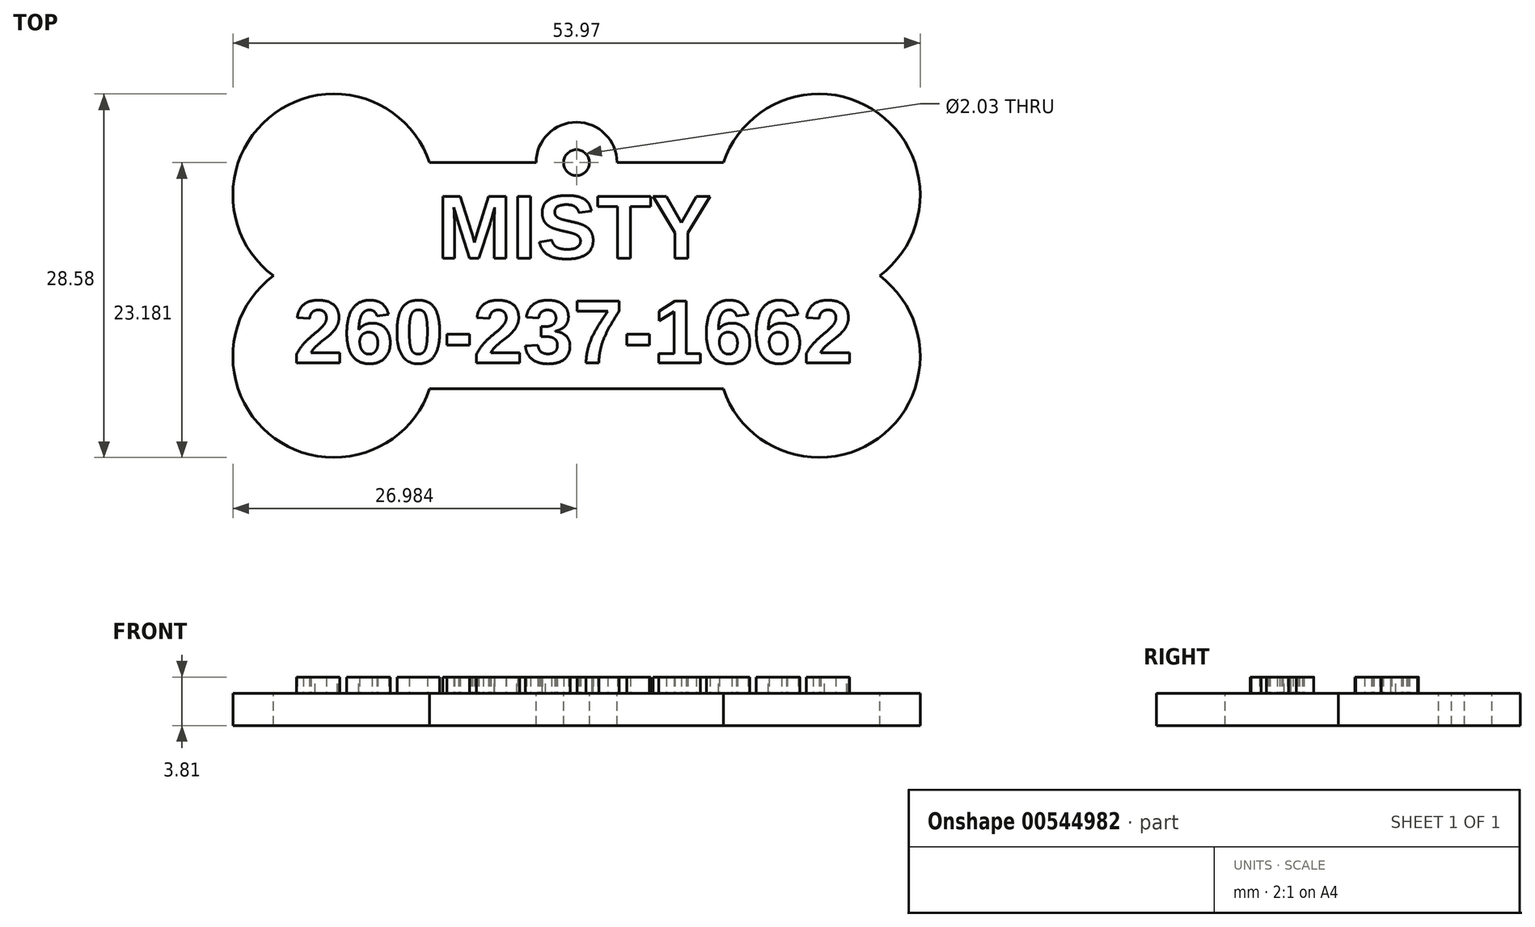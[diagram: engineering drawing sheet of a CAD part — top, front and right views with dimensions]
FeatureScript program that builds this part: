
annotation { "Feature Type Name" : "Feature", "Feature Type Description" : "" }
export const myFeature = defineFeature(function(context is Context, id is Id, definition is map)
    precondition{}
    {
        {
            var Q0;
            Q0=qCreatedBy(makeId("Top.planeOp"),FACE);
            var sketch = newSketch(context, id + "F0", { "sketchPlane" : qUnion([Q0])});
            skArc(sketch, "E0", {"start": v(-23.64, 27.3) * mm, "mid": v(-35.81, 31.18) * mm, "end": v(-35.92, 18.4) * mm});
            skArc(sketch, "E1", {"start": v(11.7, 18.4) * mm, "mid": v(11.6, 31.18) * mm, "end": v(-0.58, 27.3) * mm});
            skArc(sketch, "E2", {"start": v(-35.92, 18.4) * mm, "mid": v(-35.81, 5.62) * mm, "end": v(-23.64, 9.51) * mm});
            skArc(sketch, "E3", {"start": v(-0.58, 9.51) * mm, "mid": v(11.6, 5.62) * mm, "end": v(11.7, 18.4) * mm});
            skArc(sketch, "E4", {"start": v(-8.93, 27.3) * mm, "mid": v(-12.1, 30.47) * mm, "end": v(-15.28, 27.3) * mm});
            skLineSegment(sketch, "E5", {"start": v(-23.64, 27.3) * mm, "end": v(-15.28, 27.3) * mm});
            skLineSegment(sketch, "E6.0", {"start": v(-23.64, 9.51) * mm, "end": v(-0.58, 9.51) * mm});
            skPoint(sketch, "E7.orphan", {"position": v(-31.16, 27.3) * mm});
            skPoint(sketch, "E8.orphan", {"position": v(6.94, 27.3) * mm});
            skLineSegment(sketch, "E9.trimOffspring", {"start": v(-8.93, 27.3) * mm, "end": v(-0.58, 27.3) * mm});
            skCircle(sketch, "E10", {"center": v(-12.1, 27.3) * mm, "radius": 1.02 * mm});
            skSolve(sketch);
        }
        {
            var Q0;
            Q0=qSketchRegion(id+"F0",true);
            extrude(context, id + "F1", {"entities" : qUnion([Q0]), "oppositeDirection" : true, "depth" : 2.54 * mm, "offsetDistance" : 25.4 * mm});
        }
        {
            var Q0;
            Q0=makeQuery(id+"F1.opExtrude","CAP_FACE",FACE,{"disambiguationData":[OSD([sQuery(id+"F0.wireOp",EDGE,"E0"),sQuery(id+"F0.wireOp",EDGE,"E1"),sQuery(id+"F0.wireOp",EDGE,"E2"),sQuery(id+"F0.wireOp",EDGE,"E3"),sQuery(id+"F0.wireOp",EDGE,"E4"),sQuery(id+"F0.wireOp",EDGE,"E5"),sQuery(id+"F0.wireOp",EDGE,"E6.0"),sQuery(id+"F0.wireOp",EDGE,"E9.trimOffspring"),sQuery(id+"F0.wireOp",EDGE,"E10")])],"isStart":true});
            var sketch = newSketch(context, id + "F2", { "sketchPlane" : qUnion([Q0])});
            skText(sketch, "E11", { "text": "MISTY", "fontName": "Arimo-Bold.ttf"});
            const initialGuessF2  = {"E11": [-0.02307, 0.01978, 1, 0, 0.00508]};
            skSetInitialGuess(sketch, initialGuessF2);
            skSolve(sketch);
        }
        {
            var Q0;
            Q0=qSketchRegion(id+"F2",true);
            extrude(context, id + "F3", {"entities" : qUnion([Q0]), "operationType" : NewBodyOperationType.ADD, "depth" : 1.27 * mm, "offsetDistance" : 25.4 * mm});
        }
        {
            var Q0;
            {var subQ0=sQuery(id+"F0.wireOp",EDGE,"E6.0");var subQ1=sQuery(id+"F0.wireOp",EDGE,"E5");var subQ2=sQuery(id+"F0.wireOp",EDGE,"E0");var subQ3=sQuery(id+"F0.wireOp",EDGE,"E4");var subQ4=sQuery(id+"F0.wireOp",EDGE,"E3");var subQ5=sQuery(id+"F0.wireOp",EDGE,"E1");var subQ6=sQuery(id+"F0.wireOp",EDGE,"E2");var subQ7=sQuery(id+"F0.wireOp",EDGE,"E9.trimOffspring");var subQ8=sQuery(id+"F0.wireOp",EDGE,"E10");Q0=makeQuery(id+"F3.boolean.opBoolean","SPLIT",FACE,{"disambiguationData":[TD([makeQuery(id+"F1.opExtrude","SWEPT_FACE",FACE,{"disambiguationData":[OSD([subQ2])]})])],"derivedFrom":makeQuery(id+"F1.opExtrude","CAP_FACE",FACE,{"disambiguationData":[OSD([subQ2,subQ5,subQ6,subQ4,subQ3,subQ1,subQ0,subQ7,subQ8])],"isStart":true})});}
            var sketch = newSketch(context, id + "F4", { "sketchPlane" : qUnion([Q0])});
            skText(sketch, "E12", { "text": "260-237-1662", "fontName": "Arimo-Bold.ttf"});
            const initialGuessF4  = {"E12": [-0.03433, 0.01155, 1, 0, 0.00508]};
            skSetInitialGuess(sketch, initialGuessF4);
            skSolve(sketch);
        }
        {
            var Q0;
            Q0=qSketchRegion(id+"F4",true);
            extrude(context, id + "F5", {"entities" : qUnion([Q0]), "operationType" : NewBodyOperationType.ADD, "depth" : 1.27 * mm, "offsetDistance" : 25.4 * mm});
        }
    });
